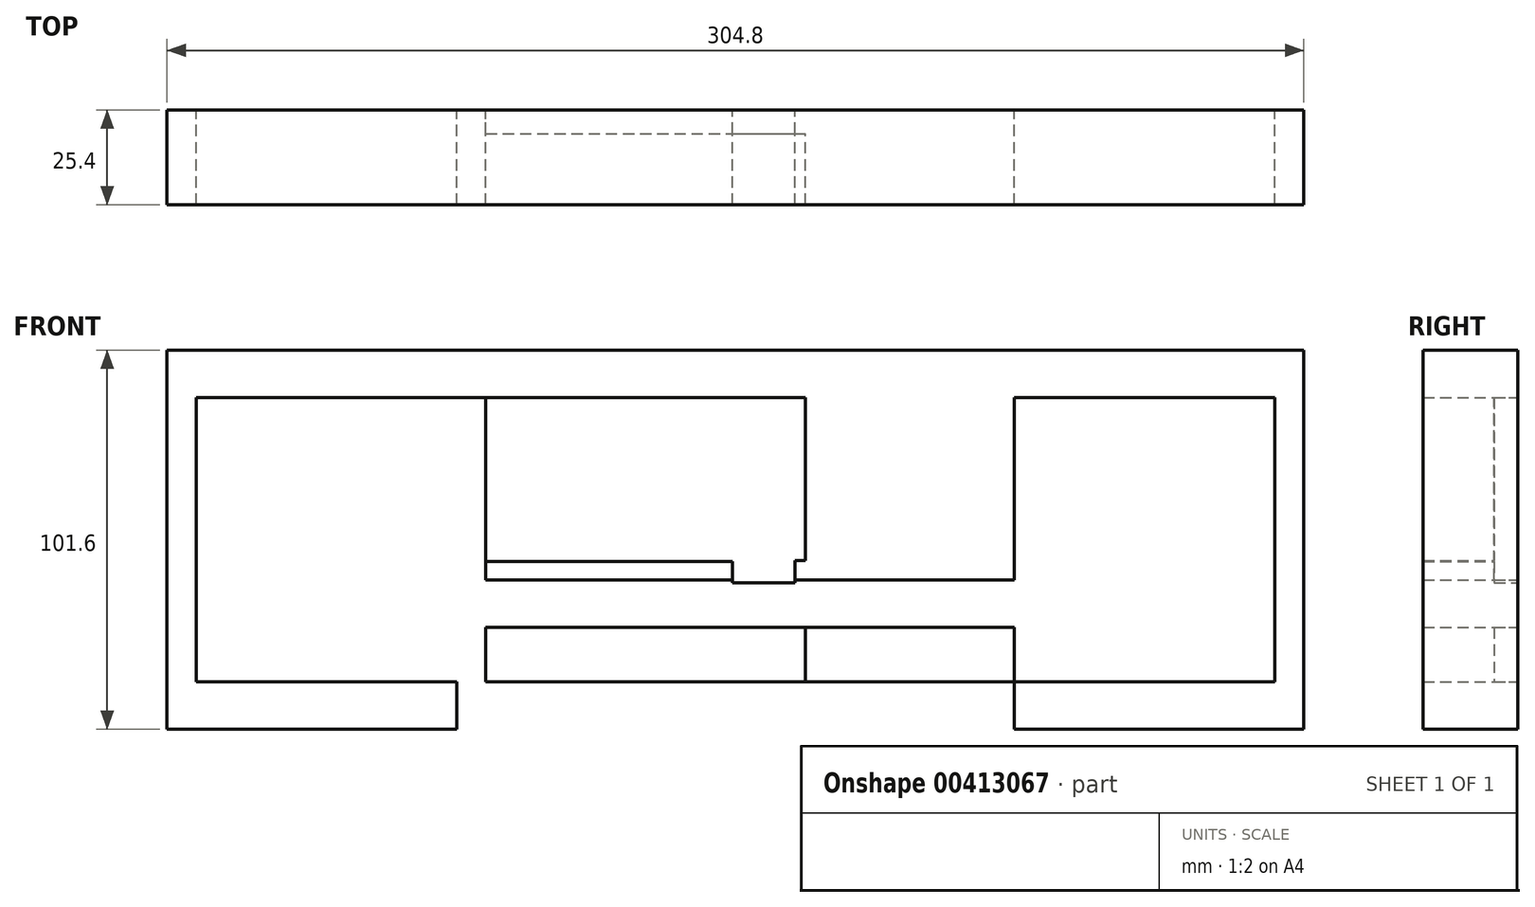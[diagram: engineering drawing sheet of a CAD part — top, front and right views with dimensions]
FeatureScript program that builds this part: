
annotation { "Feature Type Name" : "Feature", "Feature Type Description" : "" }
export const myFeature = defineFeature(function(context is Context, id is Id, definition is map)
    precondition{}
    {
        {
            var Q0;
            Q0=qCreatedBy(makeId("Front.planeOp"),FACE);
            var sketch = newSketch(context, id + "F0", { "sketchPlane" : qUnion([Q0])});
            skLineSegment(sketch, "E0.bottom", {"start": v(152.4, 59.41) * mm, "end": v(-152.4, 59.41) * mm});
            skLineSegment(sketch, "E0.top", {"start": v(152.4, -42.19) * mm, "end": v(-152.4, -42.19) * mm});
            skLineSegment(sketch, "E0.left", {"start": v(152.4, 59.41) * mm, "end": v(152.4, -42.19) * mm});
            skLineSegment(sketch, "E0.right", {"start": v(-152.4, 59.41) * mm, "end": v(-152.4, -42.19) * mm});
            skPoint(sketch, "E0.middle", {"position": v(0, 8.61) * mm});
            skLineSegment(sketch, "E1.bottom", {"start": v(-152.4, 59.41) * mm, "end": v(-144.58, 59.41) * mm});
            skLineSegment(sketch, "E1.top", {"start": v(-152.4, -42.19) * mm, "end": v(-144.58, -42.19) * mm});
            skLineSegment(sketch, "E1.right", {"start": v(-144.58, 59.41) * mm, "end": v(-144.58, -42.19) * mm});
            skLineSegment(sketch, "E2.bottom", {"start": v(152.4, 59.41) * mm, "end": v(144.58, 59.41) * mm});
            skLineSegment(sketch, "E2.top", {"start": v(152.4, -42.19) * mm, "end": v(144.58, -42.19) * mm});
            skLineSegment(sketch, "E2.right", {"start": v(144.58, 59.41) * mm, "end": v(144.58, -42.19) * mm});
            skLineSegment(sketch, "E3.bottom", {"start": v(-152.4, 59.41) * mm, "end": v(152.4, 59.41) * mm});
            skLineSegment(sketch, "E3.top", {"start": v(-152.4, 53.06) * mm, "end": v(152.4, 53.06) * mm});
            skLineSegment(sketch, "E3.left", {"start": v(-152.4, 59.41) * mm, "end": v(-152.4, 53.06) * mm});
            skLineSegment(sketch, "E3.right", {"start": v(152.4, 59.41) * mm, "end": v(152.4, 53.06) * mm});
            skLineSegment(sketch, "E4.bottom", {"start": v(-152.4, -42.19) * mm, "end": v(152.4, -42.19) * mm});
            skLineSegment(sketch, "E4.top", {"start": v(-152.4, -35.84) * mm, "end": v(152.4, -35.84) * mm});
            skLineSegment(sketch, "E4.left", {"start": v(-152.4, -42.19) * mm, "end": v(-152.4, -35.84) * mm});
            skLineSegment(sketch, "E4.right", {"start": v(152.4, -42.19) * mm, "end": v(152.4, -35.84) * mm});
            skLineSegment(sketch, "E5.bottom", {"start": v(-152.4, 59.41) * mm, "end": v(-74.73, 59.41) * mm});
            skLineSegment(sketch, "E5.top", {"start": v(-152.4, -42.19) * mm, "end": v(-74.73, -42.19) * mm});
            skLineSegment(sketch, "E5.right", {"start": v(-74.73, 59.41) * mm, "end": v(-74.73, -42.19) * mm});
            skLineSegment(sketch, "E6.bottom", {"start": v(152.4, 59.41) * mm, "end": v(74.73, 59.41) * mm});
            skLineSegment(sketch, "E6.top", {"start": v(152.4, -42.19) * mm, "end": v(74.73, -42.19) * mm});
            skLineSegment(sketch, "E6.right", {"start": v(74.73, 59.41) * mm, "end": v(74.73, -42.19) * mm});
            skLineSegment(sketch, "E7.bottom", {"start": v(74.73, -42.19) * mm, "end": v(-74.73, -42.19) * mm});
            skLineSegment(sketch, "E7.top", {"start": v(74.73, -14.88) * mm, "end": v(-74.73, -14.88) * mm});
            skLineSegment(sketch, "E7.left", {"start": v(74.73, -42.19) * mm, "end": v(74.73, -14.88) * mm});
            skLineSegment(sketch, "E7.right", {"start": v(-74.73, -42.19) * mm, "end": v(-74.73, -14.88) * mm});
            skLineSegment(sketch, "E8.bottom", {"start": v(-74.73, -14.88) * mm, "end": v(74.73, -14.88) * mm});
            skLineSegment(sketch, "E8.top", {"start": v(-74.73, -35.84) * mm, "end": v(74.73, -35.84) * mm});
            skLineSegment(sketch, "E8.left", {"start": v(-74.73, -14.88) * mm, "end": v(-74.73, -35.84) * mm});
            skLineSegment(sketch, "E8.right", {"start": v(74.73, -14.88) * mm, "end": v(74.73, -35.84) * mm});
            skLineSegment(sketch, "E9.top", {"start": v(-74.73, -2.18) * mm, "end": v(74.73, -2.18) * mm});
            skLineSegment(sketch, "E9.left", {"start": v(-74.73, -14.88) * mm, "end": v(-74.73, -2.18) * mm});
            skLineSegment(sketch, "E9.right", {"start": v(74.73, -14.88) * mm, "end": v(74.73, -2.18) * mm});
            skLineSegment(sketch, "E10.bottom", {"start": v(-74.73, -42.19) * mm, "end": v(-66.93, -42.19) * mm});
            skLineSegment(sketch, "E10.top", {"start": v(-74.73, 59.41) * mm, "end": v(-66.93, 59.41) * mm});
            skLineSegment(sketch, "E10.left", {"start": v(-74.73, -42.19) * mm, "end": v(-74.73, 59.41) * mm});
            skLineSegment(sketch, "E10.right", {"start": v(-66.93, -42.19) * mm, "end": v(-66.93, 59.41) * mm});
            skLineSegment(sketch, "E11.bottom", {"start": v(-66.93, 59.41) * mm, "end": v(18.8, 59.41) * mm});
            skLineSegment(sketch, "E11.top", {"start": v(-66.93, -42.19) * mm, "end": v(18.8, -42.19) * mm});
            skLineSegment(sketch, "E11.left", {"start": v(-66.93, 59.41) * mm, "end": v(-66.93, -42.19) * mm});
            skLineSegment(sketch, "E11.right", {"start": v(18.8, 59.41) * mm, "end": v(18.8, -42.19) * mm});
            skLineSegment(sketch, "E12.bottom", {"start": v(-66.93, 2.73) * mm, "end": v(-0.84, 2.73) * mm});
            skLineSegment(sketch, "E12.top", {"start": v(-66.93, -28.32) * mm, "end": v(-0.84, -28.32) * mm});
            skLineSegment(sketch, "E12.left", {"start": v(-66.93, 2.73) * mm, "end": v(-66.93, -28.32) * mm});
            skLineSegment(sketch, "E12.right", {"start": v(-0.84, 2.73) * mm, "end": v(-0.84, -28.32) * mm});
            skLineSegment(sketch, "E13.bottom", {"start": v(-0.84, -28.32) * mm, "end": v(15.93, -28.32) * mm});
            skLineSegment(sketch, "E13.top", {"start": v(-0.84, 3) * mm, "end": v(15.93, 3) * mm});
            skLineSegment(sketch, "E13.left", {"start": v(-0.84, -28.32) * mm, "end": v(-0.84, 3) * mm});
            skLineSegment(sketch, "E13.right", {"start": v(15.93, -28.32) * mm, "end": v(15.93, 3) * mm});
            skLineSegment(sketch, "E14.bottom", {"start": v(15.93, 3) * mm, "end": v(18.8, 3) * mm});
            skLineSegment(sketch, "E14.top", {"start": v(15.93, -28.32) * mm, "end": v(18.8, -28.32) * mm});
            skLineSegment(sketch, "E14.left", {"start": v(15.93, 3) * mm, "end": v(15.93, -28.32) * mm});
            skLineSegment(sketch, "E14.right", {"start": v(18.8, 3) * mm, "end": v(18.8, -28.32) * mm});
            skLineSegment(sketch, "E15.bottom", {"start": v(-0.84, -14.88) * mm, "end": v(15.93, -14.88) * mm});
            skLineSegment(sketch, "E15.top", {"start": v(-0.84, -2.95) * mm, "end": v(15.93, -2.95) * mm});
            skLineSegment(sketch, "E15.left", {"start": v(-0.84, -14.88) * mm, "end": v(-0.84, -2.95) * mm});
            skLineSegment(sketch, "E15.right", {"start": v(15.93, -14.88) * mm, "end": v(15.93, -2.95) * mm});
            skLineSegment(sketch, "E16.top", {"start": v(-152.4, -29.49) * mm, "end": v(152.4, -29.49) * mm});
            skLineSegment(sketch, "E16.left", {"start": v(-152.4, -42.19) * mm, "end": v(-152.4, -29.49) * mm});
            skLineSegment(sketch, "E16.right", {"start": v(152.4, -42.19) * mm, "end": v(152.4, -29.49) * mm});
            skLineSegment(sketch, "E17.top", {"start": v(-152.4, 46.71) * mm, "end": v(152.4, 46.71) * mm});
            skLineSegment(sketch, "E17.left", {"start": v(-152.4, 59.41) * mm, "end": v(-152.4, 46.71) * mm});
            skLineSegment(sketch, "E17.right", {"start": v(152.4, 59.41) * mm, "end": v(152.4, 46.71) * mm});
            skSolve(sketch);
        }
        {
            var Q0;
            {var subQ0=sQuery(id+"F0.wireOp",EDGE,"E4.bottom");var subQ1=sQuery(id+"F0.wireOp",EDGE,"E1.right");var subQ2=makeQuery(id+"F0.imprint","INTERSECT",VERTEX,{"derivedFrom":[subQ1,subQ0]});Q0=makeQuery(id+"F0.imprint","IMPRINT",FACE,{"disambiguationData":[TD([[makeQuery(id+"F0.imprint","IMPRINT",EDGE,{"disambiguationData":[TD([[subQ2,1.0]])],"derivedFrom":subQ1}),-1.0]])]});}
            var Q1;
            {var subQ0=sQuery(id+"F0.wireOp",EDGE,"E16.top");var subQ1=sQuery(id+"F0.wireOp",EDGE,"E1.right");var subQ2=makeQuery(id+"F0.imprint","INTERSECT",VERTEX,{"derivedFrom":[subQ1,subQ0]});Q1=makeQuery(id+"F0.imprint","IMPRINT",FACE,{"disambiguationData":[TD([[makeQuery(id+"F0.imprint","IMPRINT",EDGE,{"disambiguationData":[TD([[subQ2,-1.0]])],"derivedFrom":subQ1}),-1.0]])]});}
            var Q2;
            {var subQ5=sQuery(id+"F0.wireOp",EDGE,"E0.right");Q2=makeQuery(id+"F0.imprint","IMPRINT",FACE,{"disambiguationData":[TD([[makeQuery(id+"F0.imprint","IMPRINT",EDGE,{"derivedFrom":subQ5}),1.0]])]});}
            var Q3;
            {var subQ0=sQuery(id+"F0.wireOp",EDGE,"E3.top");var subQ1=sQuery(id+"F0.wireOp",EDGE,"E1.right");var subQ2=makeQuery(id+"F0.imprint","INTERSECT",VERTEX,{"derivedFrom":[subQ1,subQ0]});Q3=makeQuery(id+"F0.imprint","IMPRINT",FACE,{"disambiguationData":[TD([[makeQuery(id+"F0.imprint","IMPRINT",EDGE,{"disambiguationData":[TD([[subQ2,-1.0]])],"derivedFrom":subQ1}),-1.0]])]});}
            var Q4;
            {var subQ0=sQuery(id+"F0.wireOp",EDGE,"E3.bottom");var subQ1=sQuery(id+"F0.wireOp",EDGE,"E1.right");var subQ2=makeQuery(id+"F0.imprint","INTERSECT",VERTEX,{"derivedFrom":[subQ1,subQ0]});Q4=makeQuery(id+"F0.imprint","IMPRINT",FACE,{"disambiguationData":[TD([[makeQuery(id+"F0.imprint","IMPRINT",EDGE,{"disambiguationData":[TD([[subQ2,-1.0]])],"derivedFrom":subQ1}),-1.0]])]});}
            var Q5;
            {var subQ0=sQuery(id+"F0.wireOp",EDGE,"E4.bottom");var subQ1=sQuery(id+"F0.wireOp",EDGE,"E2.right");var subQ2=makeQuery(id+"F0.imprint","INTERSECT",VERTEX,{"derivedFrom":[subQ1,subQ0]});Q5=makeQuery(id+"F0.imprint","IMPRINT",FACE,{"disambiguationData":[TD([[makeQuery(id+"F0.imprint","IMPRINT",EDGE,{"disambiguationData":[TD([[subQ2,1.0]])],"derivedFrom":subQ1}),1.0]])]});}
            var Q6;
            {var subQ0=sQuery(id+"F0.wireOp",EDGE,"E16.top");var subQ1=sQuery(id+"F0.wireOp",EDGE,"E2.right");var subQ2=makeQuery(id+"F0.imprint","INTERSECT",VERTEX,{"derivedFrom":[subQ1,subQ0]});Q6=makeQuery(id+"F0.imprint","IMPRINT",FACE,{"disambiguationData":[TD([[makeQuery(id+"F0.imprint","IMPRINT",EDGE,{"disambiguationData":[TD([[subQ2,-1.0]])],"derivedFrom":subQ1}),1.0]])]});}
            var Q7;
            {var subQ5=sQuery(id+"F0.wireOp",EDGE,"E0.left");Q7=makeQuery(id+"F0.imprint","IMPRINT",FACE,{"disambiguationData":[TD([[makeQuery(id+"F0.imprint","IMPRINT",EDGE,{"derivedFrom":subQ5}),-1.0]])]});}
            var Q8;
            {var subQ0=sQuery(id+"F0.wireOp",EDGE,"E3.top");var subQ1=sQuery(id+"F0.wireOp",EDGE,"E2.right");var subQ2=makeQuery(id+"F0.imprint","INTERSECT",VERTEX,{"derivedFrom":[subQ1,subQ0]});Q8=makeQuery(id+"F0.imprint","IMPRINT",FACE,{"disambiguationData":[TD([[makeQuery(id+"F0.imprint","IMPRINT",EDGE,{"disambiguationData":[TD([[subQ2,-1.0]])],"derivedFrom":subQ1}),1.0]])]});}
            var Q9;
            {var subQ0=sQuery(id+"F0.wireOp",EDGE,"E3.bottom");var subQ1=sQuery(id+"F0.wireOp",EDGE,"E2.right");var subQ2=makeQuery(id+"F0.imprint","INTERSECT",VERTEX,{"derivedFrom":[subQ1,subQ0]});Q9=makeQuery(id+"F0.imprint","IMPRINT",FACE,{"disambiguationData":[TD([[makeQuery(id+"F0.imprint","IMPRINT",EDGE,{"disambiguationData":[TD([[subQ2,-1.0]])],"derivedFrom":subQ1}),1.0]])]});}
            var Q10;
            {var subQ0=sQuery(id+"F0.wireOp",EDGE,"E3.top");var subQ1=sQuery(id+"F0.wireOp",EDGE,"E1.right");var subQ2=makeQuery(id+"F0.imprint","INTERSECT",VERTEX,{"derivedFrom":[subQ1,subQ0]});Q10=makeQuery(id+"F0.imprint","IMPRINT",FACE,{"disambiguationData":[TD([[makeQuery(id+"F0.imprint","IMPRINT",EDGE,{"disambiguationData":[TD([[subQ2,-1.0]])],"derivedFrom":subQ1}),1.0]])]});}
            var Q11;
            {var subQ0=sQuery(id+"F0.wireOp",EDGE,"E3.bottom");var subQ1=sQuery(id+"F0.wireOp",EDGE,"E1.right");var subQ2=makeQuery(id+"F0.imprint","INTERSECT",VERTEX,{"derivedFrom":[subQ1,subQ0]});Q11=makeQuery(id+"F0.imprint","IMPRINT",FACE,{"disambiguationData":[TD([[makeQuery(id+"F0.imprint","IMPRINT",EDGE,{"disambiguationData":[TD([[subQ2,-1.0]])],"derivedFrom":subQ1}),1.0]])]});}
            var Q12;
            {var subQ0=sQuery(id+"F0.wireOp",EDGE,"E10.left");var subQ1=sQuery(id+"F0.wireOp",EDGE,"E3.top");var subQ2=makeQuery(id+"F0.imprint","INTERSECT",VERTEX,{"derivedFrom":[subQ1,subQ0]});Q12=makeQuery(id+"F0.imprint","IMPRINT",FACE,{"disambiguationData":[TD([[makeQuery(id+"F0.imprint","IMPRINT",EDGE,{"disambiguationData":[TD([[subQ2,-1.0]])],"derivedFrom":subQ1}),-1.0]])]});}
            var Q13;
            {var subQ0=sQuery(id+"F0.wireOp",EDGE,"E10.left");var subQ1=sQuery(id+"F0.wireOp",EDGE,"E3.top");var subQ2=makeQuery(id+"F0.imprint","INTERSECT",VERTEX,{"derivedFrom":[subQ1,subQ0]});Q13=makeQuery(id+"F0.imprint","IMPRINT",FACE,{"disambiguationData":[TD([[makeQuery(id+"F0.imprint","IMPRINT",EDGE,{"disambiguationData":[TD([[subQ2,-1.0]])],"derivedFrom":subQ1}),1.0]])]});}
            var Q14;
            {var subQ0=sQuery(id+"F0.wireOp",EDGE,"E11.right");var subQ1=sQuery(id+"F0.wireOp",EDGE,"E3.top");var subQ2=makeQuery(id+"F0.imprint","INTERSECT",VERTEX,{"derivedFrom":[subQ1,subQ0]});Q14=makeQuery(id+"F0.imprint","IMPRINT",FACE,{"disambiguationData":[TD([[makeQuery(id+"F0.imprint","IMPRINT",EDGE,{"disambiguationData":[TD([[subQ2,-1.0]])],"derivedFrom":subQ1}),-1.0]])]});}
            var Q15;
            {var subQ0=sQuery(id+"F0.wireOp",EDGE,"E11.right");var subQ1=sQuery(id+"F0.wireOp",EDGE,"E3.top");var subQ2=makeQuery(id+"F0.imprint","INTERSECT",VERTEX,{"derivedFrom":[subQ1,subQ0]});Q15=makeQuery(id+"F0.imprint","IMPRINT",FACE,{"disambiguationData":[TD([[makeQuery(id+"F0.imprint","IMPRINT",EDGE,{"disambiguationData":[TD([[subQ2,-1.0]])],"derivedFrom":subQ1}),1.0]])]});}
            var Q16;
            {var subQ0=sQuery(id+"F0.wireOp",EDGE,"E3.top");var subQ1=sQuery(id+"F0.wireOp",EDGE,"E2.right");var subQ2=makeQuery(id+"F0.imprint","INTERSECT",VERTEX,{"derivedFrom":[subQ1,subQ0]});Q16=makeQuery(id+"F0.imprint","IMPRINT",FACE,{"disambiguationData":[TD([[makeQuery(id+"F0.imprint","IMPRINT",EDGE,{"disambiguationData":[TD([[subQ2,-1.0]])],"derivedFrom":subQ1}),-1.0]])]});}
            var Q17;
            {var subQ0=sQuery(id+"F0.wireOp",EDGE,"E3.bottom");var subQ1=sQuery(id+"F0.wireOp",EDGE,"E2.right");var subQ2=makeQuery(id+"F0.imprint","INTERSECT",VERTEX,{"derivedFrom":[subQ1,subQ0]});Q17=makeQuery(id+"F0.imprint","IMPRINT",FACE,{"disambiguationData":[TD([[makeQuery(id+"F0.imprint","IMPRINT",EDGE,{"disambiguationData":[TD([[subQ2,-1.0]])],"derivedFrom":subQ1}),-1.0]])]});}
            var Q18;
            {var subQ5=sQuery(id+"F0.wireOp",EDGE,"E7.left");Q18=makeQuery(id+"F0.imprint","IMPRINT",FACE,{"disambiguationData":[TD([[makeQuery(id+"F0.imprint","IMPRINT",EDGE,{"derivedFrom":subQ5}),-1.0]])]});}
            var Q19;
            {var subQ0=sQuery(id+"F0.wireOp",EDGE,"E16.top");var subQ1=sQuery(id+"F0.wireOp",EDGE,"E2.right");var subQ2=makeQuery(id+"F0.imprint","INTERSECT",VERTEX,{"derivedFrom":[subQ1,subQ0]});Q19=makeQuery(id+"F0.imprint","IMPRINT",FACE,{"disambiguationData":[TD([[makeQuery(id+"F0.imprint","IMPRINT",EDGE,{"disambiguationData":[TD([[subQ2,-1.0]])],"derivedFrom":subQ1}),-1.0]])]});}
            var Q20;
            {var subQ1=sQuery(id+"F0.wireOp",EDGE,"E8.top");var subQ3=sQuery(id+"F0.wireOp",EDGE,"E11.right");var subQ4=makeQuery(id+"F0.imprint","INTERSECT",VERTEX,{"derivedFrom":[subQ1,subQ3]});Q20=makeQuery(id+"F0.imprint","IMPRINT",FACE,{"disambiguationData":[TD([[makeQuery(id+"F0.imprint","IMPRINT",EDGE,{"disambiguationData":[TD([[subQ4,1.0]])],"derivedFrom":subQ3}),1.0]])]});}
            var Q21;
            {var subQ0=sQuery(id+"F0.wireOp",EDGE,"E7.left");Q21=makeQuery(id+"F0.imprint","IMPRINT",FACE,{"disambiguationData":[TD([[makeQuery(id+"F0.imprint","IMPRINT",EDGE,{"derivedFrom":subQ0}),1.0]])]});}
            var Q22;
            {var subQ0=sQuery(id+"F0.wireOp",EDGE,"E11.left");var subQ1=sQuery(id+"F0.wireOp",EDGE,"E8.top");var subQ2=makeQuery(id+"F0.imprint","INTERSECT",VERTEX,{"derivedFrom":[subQ1,subQ0]});Q22=makeQuery(id+"F0.imprint","IMPRINT",FACE,{"disambiguationData":[TD([[makeQuery(id+"F0.imprint","IMPRINT",EDGE,{"disambiguationData":[TD([[subQ2,-1.0]])],"derivedFrom":subQ1}),-1.0]])]});}
            var Q23;
            {var subQ3=sQuery(id+"F0.wireOp",EDGE,"E11.left");var subQ5=sQuery(id+"F0.wireOp",EDGE,"E4.bottom");var subQ7=makeQuery(id+"F0.imprint","INTERSECT",VERTEX,{"derivedFrom":[subQ3,subQ5]});Q23=makeQuery(id+"F0.imprint","IMPRINT",FACE,{"disambiguationData":[TD([[makeQuery(id+"F0.imprint","IMPRINT",EDGE,{"disambiguationData":[TD([[subQ7,1.0]])],"derivedFrom":subQ3}),-1.0]])]});}
            var Q24;
            {var subQ1=sQuery(id+"F0.wireOp",EDGE,"E8.top");var subQ3=sQuery(id+"F0.wireOp",EDGE,"E11.left");var subQ4=makeQuery(id+"F0.imprint","INTERSECT",VERTEX,{"derivedFrom":[subQ1,subQ3]});Q24=makeQuery(id+"F0.imprint","IMPRINT",FACE,{"disambiguationData":[TD([[makeQuery(id+"F0.imprint","IMPRINT",EDGE,{"disambiguationData":[TD([[subQ4,1.0]])],"derivedFrom":subQ3}),-1.0]])]});}
            var Q25;
            {var subQ0=sQuery(id+"F0.wireOp",EDGE,"E4.bottom");var subQ1=sQuery(id+"F0.wireOp",EDGE,"E1.right");var subQ2=makeQuery(id+"F0.imprint","INTERSECT",VERTEX,{"derivedFrom":[subQ1,subQ0]});Q25=makeQuery(id+"F0.imprint","IMPRINT",FACE,{"disambiguationData":[TD([[makeQuery(id+"F0.imprint","IMPRINT",EDGE,{"disambiguationData":[TD([[subQ2,1.0]])],"derivedFrom":subQ1}),1.0]])]});}
            var Q26;
            {var subQ0=sQuery(id+"F0.wireOp",EDGE,"E16.top");var subQ1=sQuery(id+"F0.wireOp",EDGE,"E1.right");var subQ2=makeQuery(id+"F0.imprint","INTERSECT",VERTEX,{"derivedFrom":[subQ1,subQ0]});Q26=makeQuery(id+"F0.imprint","IMPRINT",FACE,{"disambiguationData":[TD([[makeQuery(id+"F0.imprint","IMPRINT",EDGE,{"disambiguationData":[TD([[subQ2,-1.0]])],"derivedFrom":subQ1}),1.0]])]});}
            var Q27;
            {var subQ5=sQuery(id+"F0.wireOp",EDGE,"E8.right");var subQ7=sQuery(id+"F0.wireOp",EDGE,"E16.top");var subQ9=makeQuery(id+"F0.imprint","INTERSECT",VERTEX,{"derivedFrom":[subQ5,subQ7]});Q27=makeQuery(id+"F0.imprint","IMPRINT",FACE,{"disambiguationData":[TD([[makeQuery(id+"F0.imprint","IMPRINT",EDGE,{"disambiguationData":[TD([[subQ9,1.0]])],"derivedFrom":subQ7}),1.0]])]});}
            var Q28;
            {var subQ0=sQuery(id+"F0.wireOp",EDGE,"E9.right");Q28=makeQuery(id+"F0.imprint","IMPRINT",FACE,{"disambiguationData":[TD([[makeQuery(id+"F0.imprint","IMPRINT",EDGE,{"derivedFrom":subQ0}),1.0]])]});}
            var Q29;
            {var subQ5=sQuery(id+"F0.wireOp",EDGE,"E17.top");var subQ7=sQuery(id+"F0.wireOp",EDGE,"E6.right");var subQ9=makeQuery(id+"F0.imprint","INTERSECT",VERTEX,{"derivedFrom":[subQ7,subQ5]});Q29=makeQuery(id+"F0.imprint","IMPRINT",FACE,{"disambiguationData":[TD([[makeQuery(id+"F0.imprint","IMPRINT",EDGE,{"disambiguationData":[TD([[subQ9,1.0]])],"derivedFrom":subQ5}),-1.0]])]});}
            var Q30;
            {var subQ3=sQuery(id+"F0.wireOp",EDGE,"E8.bottom");var subQ5=sQuery(id+"F0.wireOp",EDGE,"E10.left");var subQ6=makeQuery(id+"F0.imprint","INTERSECT",VERTEX,{"derivedFrom":[subQ3,subQ5]});Q30=makeQuery(id+"F0.imprint","IMPRINT",FACE,{"disambiguationData":[TD([[makeQuery(id+"F0.imprint","IMPRINT",EDGE,{"disambiguationData":[TD([[subQ6,-1.0]])],"derivedFrom":subQ3}),-1.0]])]});}
            var Q31;
            {var subQ0=sQuery(id+"F0.wireOp",EDGE,"E10.left");var subQ1=sQuery(id+"F0.wireOp",EDGE,"E8.bottom");var subQ2=makeQuery(id+"F0.imprint","INTERSECT",VERTEX,{"derivedFrom":[subQ1,subQ0]});Q31=makeQuery(id+"F0.imprint","IMPRINT",FACE,{"disambiguationData":[TD([[makeQuery(id+"F0.imprint","IMPRINT",EDGE,{"disambiguationData":[TD([[subQ2,-1.0]])],"derivedFrom":subQ1}),1.0]])]});}
            var Q32;
            {var subQ3=sQuery(id+"F0.wireOp",EDGE,"E9.top");var subQ7=sQuery(id+"F0.wireOp",EDGE,"E10.left");var subQ8=makeQuery(id+"F0.imprint","INTERSECT",VERTEX,{"derivedFrom":[subQ3,subQ7]});Q32=makeQuery(id+"F0.imprint","IMPRINT",FACE,{"disambiguationData":[TD([[makeQuery(id+"F0.imprint","IMPRINT",EDGE,{"disambiguationData":[TD([[subQ8,-1.0]])],"derivedFrom":subQ3}),1.0]])]});}
            extrude(context, id + "F1", {"entities" : qUnion([Q0, Q1, Q2, Q3, Q4, Q5, Q6, Q7, Q8, Q9, Q10, Q11, Q12, Q13, Q14, Q15, Q16, Q17, Q18, Q19, Q20, Q21, Q22, Q23, Q24, Q25, Q26, Q27, Q28, Q29, Q30, Q31, Q32]), "depth" : 25.4 * mm});
        }
        {
            var Q0;
            {var subQ5=sQuery(id+"F0.wireOp",EDGE,"E15.top");Q0=makeQuery(id+"F0.imprint","IMPRINT",FACE,{"disambiguationData":[TD([[makeQuery(id+"F0.imprint","IMPRINT",EDGE,{"derivedFrom":subQ5}),1.0]])]});}
            var Q1;
            {var subQ0=sQuery(id+"F0.wireOp",EDGE,"E13.bottom");Q1=makeQuery(id+"F0.imprint","IMPRINT",FACE,{"disambiguationData":[TD([[makeQuery(id+"F0.imprint","IMPRINT",EDGE,{"derivedFrom":subQ0}),1.0]])]});}
            var Q2;
            {var subQ4=sQuery(id+"F0.wireOp",EDGE,"E12.top");Q2=makeQuery(id+"F0.imprint","IMPRINT",FACE,{"disambiguationData":[TD([[makeQuery(id+"F0.imprint","IMPRINT",EDGE,{"derivedFrom":subQ4}),-1.0]])]});}
            var Q3;
            {var subQ0=sQuery(id+"F0.wireOp",EDGE,"E11.left");var subQ1=sQuery(id+"F0.wireOp",EDGE,"E8.top");var subQ2=makeQuery(id+"F0.imprint","INTERSECT",VERTEX,{"derivedFrom":[subQ1,subQ0]});Q3=makeQuery(id+"F0.imprint","IMPRINT",FACE,{"disambiguationData":[TD([[makeQuery(id+"F0.imprint","IMPRINT",EDGE,{"disambiguationData":[TD([[subQ2,-1.0]])],"derivedFrom":subQ1}),1.0]])]});}
            var Q4;
            {var subQ5=sQuery(id+"F0.wireOp",EDGE,"E12.top");Q4=makeQuery(id+"F0.imprint","IMPRINT",FACE,{"disambiguationData":[TD([[makeQuery(id+"F0.imprint","IMPRINT",EDGE,{"derivedFrom":subQ5}),1.0]])]});}
            var Q5;
            {var subQ5=sQuery(id+"F0.wireOp",EDGE,"E14.top");Q5=makeQuery(id+"F0.imprint","IMPRINT",FACE,{"disambiguationData":[TD([[makeQuery(id+"F0.imprint","IMPRINT",EDGE,{"derivedFrom":subQ5}),1.0]])]});}
            var Q6;
            {var subQ5=sQuery(id+"F0.wireOp",EDGE,"E15.right");Q6=makeQuery(id+"F0.imprint","IMPRINT",FACE,{"disambiguationData":[TD([[makeQuery(id+"F0.imprint","IMPRINT",EDGE,{"derivedFrom":subQ5}),-1.0]])]});}
            var Q7;
            {var subQ0=sQuery(id+"F0.wireOp",EDGE,"E15.left");Q7=makeQuery(id+"F0.imprint","IMPRINT",FACE,{"disambiguationData":[TD([[makeQuery(id+"F0.imprint","IMPRINT",EDGE,{"derivedFrom":subQ0}),1.0]])]});}
            var Q8;
            {var subQ5=sQuery(id+"F0.wireOp",EDGE,"E12.bottom");Q8=makeQuery(id+"F0.imprint","IMPRINT",FACE,{"disambiguationData":[TD([[makeQuery(id+"F0.imprint","IMPRINT",EDGE,{"derivedFrom":subQ5}),-1.0]])]});}
            var Q9;
            {var subQ2=sQuery(id+"F0.wireOp",EDGE,"E13.top");Q9=makeQuery(id+"F0.imprint","IMPRINT",FACE,{"disambiguationData":[TD([[makeQuery(id+"F0.imprint","IMPRINT",EDGE,{"derivedFrom":subQ2}),-1.0]])]});}
            var Q10;
            {var subQ5=sQuery(id+"F0.wireOp",EDGE,"E14.bottom");Q10=makeQuery(id+"F0.imprint","IMPRINT",FACE,{"disambiguationData":[TD([[makeQuery(id+"F0.imprint","IMPRINT",EDGE,{"derivedFrom":subQ5}),-1.0]])]});}
            var Q11;
            {var subQ7=sQuery(id+"F0.wireOp",EDGE,"E12.bottom");Q11=makeQuery(id+"F0.imprint","IMPRINT",FACE,{"disambiguationData":[TD([[makeQuery(id+"F0.imprint","IMPRINT",EDGE,{"derivedFrom":subQ7}),1.0]])]});}
            var Q12;
            {var subQ0=sQuery(id+"F0.wireOp",EDGE,"E11.left");var subQ1=sQuery(id+"F0.wireOp",EDGE,"E3.top");var subQ2=makeQuery(id+"F0.imprint","INTERSECT",VERTEX,{"derivedFrom":[subQ1,subQ0]});Q12=makeQuery(id+"F0.imprint","IMPRINT",FACE,{"disambiguationData":[TD([[makeQuery(id+"F0.imprint","IMPRINT",EDGE,{"disambiguationData":[TD([[subQ2,-1.0]])],"derivedFrom":subQ1}),-1.0]])]});}
            var Q13;
            {var subQ0=sQuery(id+"F0.wireOp",EDGE,"E11.left");var subQ1=sQuery(id+"F0.wireOp",EDGE,"E3.top");var subQ2=makeQuery(id+"F0.imprint","INTERSECT",VERTEX,{"derivedFrom":[subQ1,subQ0]});Q13=makeQuery(id+"F0.imprint","IMPRINT",FACE,{"disambiguationData":[TD([[makeQuery(id+"F0.imprint","IMPRINT",EDGE,{"disambiguationData":[TD([[subQ2,-1.0]])],"derivedFrom":subQ1}),1.0]])]});}
            extrude(context, id + "F2", {"entities" : qUnion([Q0, Q1, Q2, Q3, Q4, Q5, Q6, Q7, Q8, Q9, Q10, Q11, Q12, Q13]), "operationType" : NewBodyOperationType.ADD, "depth" : 6.35 * mm});
        }
    });
